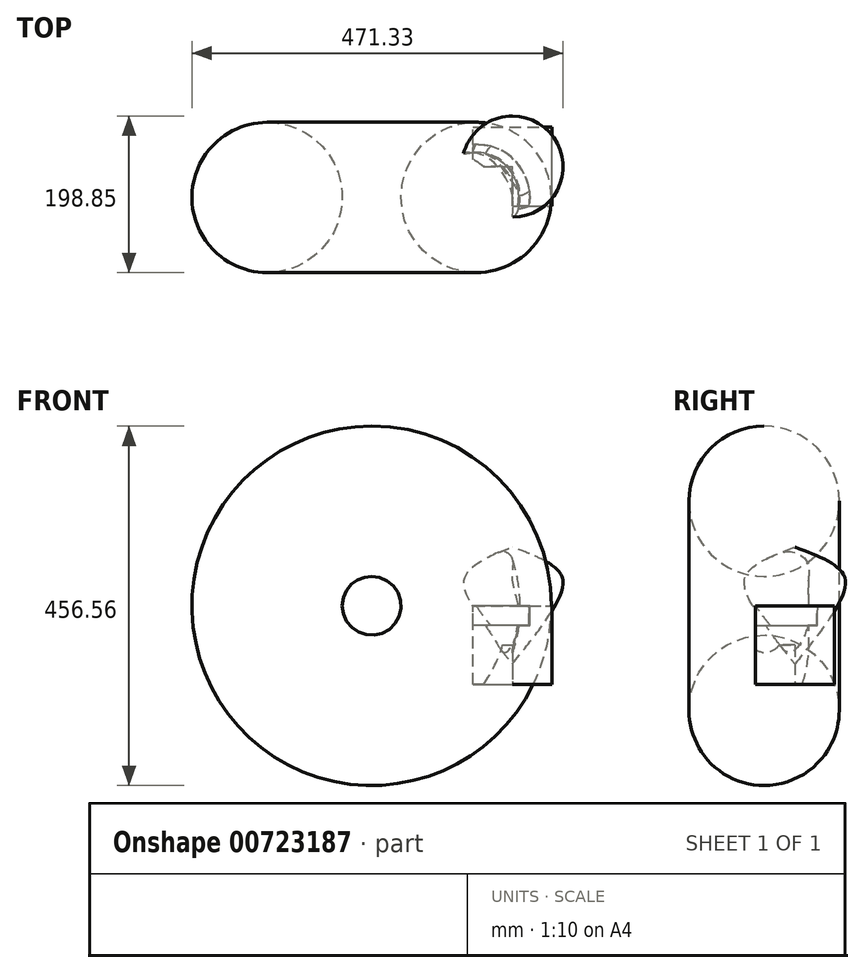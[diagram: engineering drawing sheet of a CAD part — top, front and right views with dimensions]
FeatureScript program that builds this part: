
annotation { "Feature Type Name" : "Feature", "Feature Type Description" : "" }
export const myFeature = defineFeature(function(context is Context, id is Id, definition is map)
    precondition{}
    {
        {
            var Q0;
            Q0=qCreatedBy(makeId("Top.planeOp"),FACE);
            var sketch = newSketch(context, id + "F0", { "sketchPlane" : qUnion([Q0])});
            skLineSegment(sketch, "E0.bottom", {"start": v(-50, -50) * mm, "end": v(50, -50) * mm});
            skLineSegment(sketch, "E0.top", {"start": v(-50, 50) * mm, "end": v(50, 50) * mm});
            skLineSegment(sketch, "E0.left", {"start": v(-50, -50) * mm, "end": v(-50, 50) * mm});
            skLineSegment(sketch, "E0.right", {"start": v(50, -50) * mm, "end": v(50, 50) * mm});
            skPoint(sketch, "E0.middle", {"position": v(0, 0) * mm});
            skSolve(sketch);
        }
        {
            var Q0;
            Q0 = qSketchRegion(id + "F0", true);
            extrude(context, id + "F1", {"entities" : qUnion([Q0]), "oppositeDirection" : true, "depth" : 100 * mm, "offsetDistance" : 25 * mm});
        }
        {
            var Q0;
            Q0=makeQuery(id+"F1.opExtrude","CAP_FACE",FACE,{"disambiguationData":[OSD([sQuery(id+"F0.wireOp",EDGE,"E0.bottom"),sQuery(id+"F0.wireOp",EDGE,"E0.top"),sQuery(id+"F0.wireOp",EDGE,"E0.left"),sQuery(id+"F0.wireOp",EDGE,"E0.right")])],"isStart":false});
            var sketch = newSketch(context, id + "F2", { "sketchPlane" : qUnion([Q0])});
            skLineSegment(sketch, "E1.bottom", {"start": v(-100, 100) * mm, "end": v(0, 100) * mm});
            skLineSegment(sketch, "E1.top", {"start": v(-100, 0) * mm, "end": v(0, 0) * mm});
            skLineSegment(sketch, "E1.left", {"start": v(-100, 100) * mm, "end": v(-100, 0) * mm});
            skLineSegment(sketch, "E1.right", {"start": v(0, 100) * mm, "end": v(0, 0) * mm});
            skPoint(sketch, "E1.middle", {"position": v(-50, 50) * mm});
            skSolve(sketch);
        }
        {
            var Q0;
            {var subQ1=sQuery(id+"F2.wireOp",EDGE,"E1.bottom");Q0=makeQuery(id+"F2.imprint","IMPRINT",FACE,{"disambiguationData":[TD([[makeQuery(id+"F2.imprint","IMPRINT",EDGE,{"derivedFrom":subQ1}),-1.0]])]});}
            extrude(context, id + "F3", {"entities" : qUnion([Q0]), "operationType" : NewBodyOperationType.REMOVE, "oppositeDirection" : true, "depth" : 50 * mm, "offsetDistance" : 25 * mm});
        }
        {
            var Q0;
            Q0=makeQuery(id+"F1.opExtrude","CAP_FACE",FACE,{"disambiguationData":[OSD([sQuery(id+"F0.wireOp",EDGE,"E0.bottom"),sQuery(id+"F0.wireOp",EDGE,"E0.top"),sQuery(id+"F0.wireOp",EDGE,"E0.left"),sQuery(id+"F0.wireOp",EDGE,"E0.right")])],"isStart":false});
            var sketch = newSketch(context, id + "F4", { "sketchPlane" : qUnion([Q0])});
            skLineSegment(sketch, "E2.bottom", {"start": v(-84.64, 85.8) * mm, "end": v(-15.36, 85.8) * mm});
            skLineSegment(sketch, "E2.top", {"start": v(-84.64, 14.2) * mm, "end": v(-15.36, 14.2) * mm});
            skLineSegment(sketch, "E2.left", {"start": v(-84.64, 85.8) * mm, "end": v(-84.64, 14.2) * mm});
            skLineSegment(sketch, "E2.right", {"start": v(-15.36, 85.8) * mm, "end": v(-15.36, 14.2) * mm});
            skPoint(sketch, "E2.middle", {"position": v(-50, 50) * mm});
            skSolve(sketch);
        }
        {
            var Q0;
            {var subQ1=sQuery(id+"F4.wireOp",EDGE,"E2.bottom");Q0=makeQuery(id+"F4.imprint","IMPRINT",FACE,{"disambiguationData":[TD([[makeQuery(id+"F4.imprint","IMPRINT",EDGE,{"derivedFrom":subQ1}),-1.0]])]});}
            extrude(context, id + "F5", {"entities" : qUnion([Q0]), "operationType" : NewBodyOperationType.REMOVE, "oppositeDirection" : true, "depth" : 50 * mm, "offsetDistance" : 25 * mm});
        }
        {
            var Q0;
            Q0 = qSketchRegion(id + "F2", true);
            extrude(context, id + "F6", {"entities" : qUnion([Q0]), "operationType" : NewBodyOperationType.REMOVE, "oppositeDirection" : true, "depth" : 50 * mm, "offsetDistance" : 25 * mm});
        }
        {
            var Q0;
            Q0=qCreatedBy(makeId("Right.planeOp"),FACE);
            var sketch = newSketch(context, id + "F7", { "sketchPlane" : qUnion([Q0])});
            skLineSegment(sketch, "E3", {"start": v(0, 74.43) * mm, "end": v(0, -74.06) * mm});
            skFitSpline(sketch, "E4", {"points": [v(0, 74.43) * mm, v(49.96, 51.79) * mm, v(64.17, 26.51) * mm, v(0, -74.06) * mm], "startDerivative": vector(179.16, -66.17) * mm, "endDerivative": vector(-202.28, -252.67) * mm});
            skSolve(sketch);
        }
        {
            var Q0;
            Q0 = qSketchRegion(id + "F7", true);
            var Q1;
            Q1=sQuery(id+"F7.wireOp",EDGE,"E3");
            revolve(context, id + "F8", {"surfaceOperationType" : NewSurfaceOperationType.NEW, "entities" : qUnion([Q0]), "axis" : qUnion([Q1]), "revolveType" : RevolveType.FULL});
        }
        {
            var Q0;
            Q0=qCreatedBy(makeId("Top.planeOp"),FACE);
            var sketch = newSketch(context, id + "F9", { "sketchPlane" : qUnion([Q0])});
            skCircle(sketch, "E5", {"center": v(-45.94, -39.1) * mm, "radius": 95.46 * mm});
            skSolve(sketch);
        }
        {
            var Q0;
            Q0=makeQuery(id+"F9.imprint","IMPRINT",FACE,{"disambiguationData":[TD([[makeQuery(id+"F9.imprint","IMPRINT",EDGE,{"derivedFrom":sQuery(id+"F9.wireOp",EDGE,"E5")}),1.0]])]});
            var sketch = newSketch(context, id + "F10", { "sketchPlane" : qUnion([Q0])});
            skCircle(sketch, "E6", {"center": v(-45.42, -39.1) * mm, "radius": 67.49 * mm});
            skSolve(sketch);
        }
        {
            var Q0;
            Q0 = qSketchRegion(id + "F10", true);
            extrude(context, id + "F11", {"entities" : qUnion([Q0]), "operationType" : NewBodyOperationType.REMOVE, "oppositeDirection" : true, "depth" : 25 * mm, "offsetDistance" : 25 * mm});
        }
        {
            var Q0;
            Q0=makeQuery(id+"F9.imprint","IMPRINT",FACE,{"disambiguationData":[TD([[makeQuery(id+"F9.imprint","IMPRINT",EDGE,{"derivedFrom":sQuery(id+"F9.wireOp",EDGE,"E5")}),1.0]])]});
            var sketch = newSketch(context, id + "F12", { "sketchPlane" : qUnion([Q0])});
            skCircle(sketch, "E7", {"center": v(-46.13, -37.8) * mm, "radius": 55.88 * mm});
            skLineSegment(sketch, "E8", {"start": v(-178.76, -9.6) * mm, "end": v(-178.76, -173.52) * mm});
            skCircle(sketch, "E9", {"center": v(-46.13, -37.8) * mm, "radius": 122.33 * mm});
            skSolve(sketch);
        }
        {
            var Q0;
            Q0=makeQuery(id+"F12.imprint","IMPRINT",FACE,{"disambiguationData":[TD([[makeQuery(id+"F12.imprint","IMPRINT",EDGE,{"derivedFrom":sQuery(id+"F12.wireOp",EDGE,"E7")}),1.0]])]});
            extrude(context, id + "F13", {"entities" : qUnion([Q0]), "operationType" : NewBodyOperationType.REMOVE, "oppositeDirection" : true, "depth" : 25 * mm, "offsetDistance" : 25 * mm});
        }
        {
            var Q0;
            Q0=makeQuery(id+"F12.imprint","IMPRINT",FACE,{"disambiguationData":[TD([[makeQuery(id+"F12.imprint","IMPRINT",EDGE,{"derivedFrom":sQuery(id+"F12.wireOp",EDGE,"E7")}),1.0]])]});
            extrude(context, id + "F14", {"entities" : qUnion([Q0]), "operationType" : NewBodyOperationType.REMOVE, "oppositeDirection" : true, "depth" : 25 * mm, "offsetDistance" : 25 * mm});
        }
        {
            var Q0;
            Q0=makeQuery(id+"F12.imprint","IMPRINT",FACE,{"disambiguationData":[TD([[makeQuery(id+"F12.imprint","IMPRINT",EDGE,{"derivedFrom":sQuery(id+"F12.wireOp",EDGE,"E7")}),1.0]])]});
            var Q1;
            Q1=sQuery(id+"F12.wireOp",EDGE,"E8");
            revolve(context, id + "F15", {"operationType" : NewBodyOperationType.REMOVE, "surfaceOperationType" : NewSurfaceOperationType.NEW, "entities" : qUnion([Q0]), "axis" : qUnion([Q1]), "revolveType" : RevolveType.FULL, "oppositeDirection" : true});
        }
        {
            var Q0;
            Q0=makeQuery(id+"F9.imprint","IMPRINT",FACE,{"disambiguationData":[TD([[makeQuery(id+"F9.imprint","IMPRINT",EDGE,{"derivedFrom":sQuery(id+"F9.wireOp",EDGE,"E5")}),1.0]])]});
            var Q1;
            Q1=sQuery(id+"F12.wireOp",EDGE,"E8");
            revolve(context, id + "F16", {"surfaceOperationType" : NewSurfaceOperationType.NEW, "entities" : qUnion([Q0]), "axis" : qUnion([Q1]), "revolveType" : RevolveType.FULL});
        }
        {
            var Q0;
            Q0=sQuery(id+"F12.wireOp",EDGE,"E7");
            var Q1;
            Q1=sQuery(id+"F12.wireOp",EDGE,"E8");
            revolve(context, id + "F17", {"bodyType" : ToolBodyType.SURFACE, "surfaceOperationType" : NewSurfaceOperationType.NEW, "surfaceEntities" : qUnion([Q0]), "axis" : qUnion([Q1]), "revolveType" : RevolveType.FULL});
        }
    });
